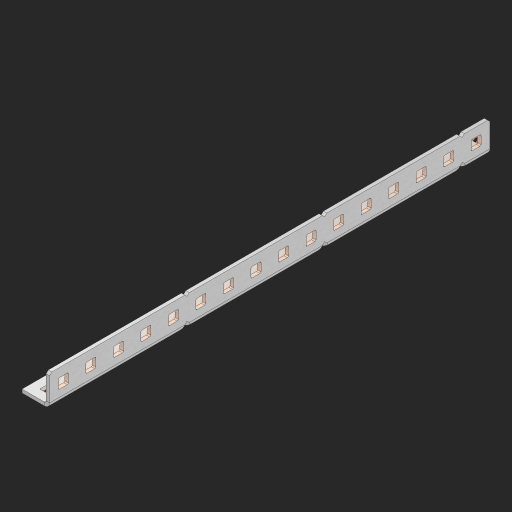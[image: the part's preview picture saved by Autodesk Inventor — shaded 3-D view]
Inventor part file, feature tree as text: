
AUTODESK INVENTOR PART (.ipt)
format: ipt  version: 2023 (Build 270158000, 158)  size: 696,832 bytes
history: native  units: in
note: dims shown in document units (in); Inventor stores cm internally (conversion verified against a paired STEP export)
features: other x37, extrude x31, sheet_metal_op x10, sketch x8, mirror x1, pattern_linear x1, chamfer x1
ambient origin geometry x8: Origin, YZ Plane, XZ Plane, XY Plane, X Axis, Y Axis, Z Axis, Center Point
bodies: Solid1 (feature_tree), Body (feature_tree)
feature tree (89):
  other  "Flange Pattern Plane"
  sheet_metal_op  "Flange Pattern"
  sheet_metal_op  "Body Pattern"
  other  "Arc Length"
  mirror  "Notch Mirror"
  pattern_linear  "Notch Pattern"  Spacing1=0.25in  [1 undecoded]
  chamfer  "End Chamfer"
  extrude  "Half Cut"  Depth=0.0625in
  sketch  "Sketch1"  dims[d0=1.5in]
  other  "Plate1"
  sketch  "Sketch2"  dims[d1=8.0in]
  other  "Plate2"
  sheet_metal_op  "Bend1"
  sheet_metal_op  "Corner1"
  sketch  "Sketch3"  dims[d2=0.0625in]
  other  "Flange Pattern Sketch"
  sketch  "Sketch7"  dims[d3=0.0625in]
  other  "Srf1"
  other  "Srf2"
  sketch  "Sketch8"  dims[d4=0.0312in]
  sketch  "Sketch9"  dims[d5=0.125in]
  other  "Srf91"
  sheet_metal_op  "Body Pattern Sketch"
  other  "Srf92"
  sketch  "Sketch13"  dims[d6=0.0625in]
  sketch  "Sketch14"  dims[d7=0.5in d8=90.0deg d9=0.0312in d10=0.25in d11=0.0625in d12=0.0625in d16=0.182in d17=0.02in d18=0.0625in d19=0.0in d20=0.25in d21=0.25in d46=0.172in d47=1.0in d48=0.0in d49=0.182in d50=0.02in d51=0.25in d52=0.25in d53=0.0625in d54=0.0in d55=0.172in d56=1.0in d57=0.0in d60=6.2992in d62=0.5in d63=0.3937in d65=0.5in d85=0.1473in d86=0.1782in d88=0.04in d89=0.0625in d90=0.0in d91=0.04in d92=0.0491in d95=2.5in d96=0.04in d97=0.25in d98=45.0deg d101=0.0in d102=2.497in d131=0.5in d132=6.2992in d134=0.5in d139=0.5in]
  other  "Srf856"
  other  "Srf1310"
  other  "Srf1311"
  other  "Srf1312"
  other  "Srf1376"
  other  "Srf1377"
  other  "Srf1728"
  other  "Srf1755"
  other  "Srf1878"
  other  "Srf1879"
  other  "Srf1880"
  other  "Srf1881"
  other  "Srf1882"
  other  "Srf1883"
  other  "Srf1884"
  other  "Srf1885"
  other  "Srf1886"
  other  "Srf1887"
  other  "Srf1942"
  other  "Srf1943"
  other  "Srf1944"
  other  "Srf1945"
  other  "Srf1946"
  other  "Srf1947"
  other  "Srf1948"
  other  "Srf1949"
  other  "Srf1950"
  other  "Srf1951"
  sheet_metal_op  "Flange Stamp"
  sheet_metal_op  "Flange Circle"
  sheet_metal_op  "Body Stamp"
  sheet_metal_op  "Body Circle"
  sheet_metal_op  "Notch"
  extrude  "ExtrusionSrf2"  Depth=0.0625in
  extrude  "ExtrusionSrf92"  Depth=0.5in
  extrude  "ExtrusionSrf856"  Depth=0.02in
  extrude  "ExtrusionSrf1310"  Depth=0.0625in
  extrude  "ExtrusionSrf1311"  TaperAngle=0.0deg  [1 undecoded]
  extrude  "ExtrusionSrf1312"  Depth=0.5in
  extrude  "ExtrusionSrf1376"  Depth=0.5in
  extrude  "ExtrusionSrf1377"  Depth=0.5in
  extrude  "ExtrusionSrf1728"  Depth=0.5in TaperAngle=0.0deg
  extrude  "ExtrusionSrf1755"  Depth=0.5in
  extrude  "ExtrusionSrf1878"  Depth=0.02in
  extrude  "ExtrusionSrf1879"  Depth=0.5in
  extrude  "ExtrusionSrf1880"  Depth=0.5in
  extrude  "ExtrusionSrf1881"  Depth=0.0625in
  extrude  "ExtrusionSrf1882"  TaperAngle=0.0deg  [1 undecoded]
  extrude  "ExtrusionSrf1883"  Depth=0.5in
  extrude  "ExtrusionSrf1884"  Depth=0.5in TaperAngle=0.0deg
  extrude  "ExtrusionSrf1885"  Depth=0.5in
  extrude  "ExtrusionSrf1886"  Depth=0.5in
  extrude  "ExtrusionSrf1887"  Depth=0.5in
  extrude  "ExtrusionSrf1942"  Depth=0.5in
  extrude  "ExtrusionSrf1943"  Depth=0.5in
  extrude  "ExtrusionSrf1944"  Depth=0.0625in
  extrude  "ExtrusionSrf1945"  TaperAngle=0.0deg  [1 undecoded]
  extrude  "ExtrusionSrf1946"  Depth=0.5in
  extrude  "ExtrusionSrf1947"  Depth=0.5in
  extrude  "ExtrusionSrf1948"  Depth=0.5in
  extrude  "ExtrusionSrf1949"  Depth=0.5in TaperAngle=45.0deg
  extrude  "ExtrusionSrf1950"  TaperAngle=0.0deg  [1 undecoded]
  extrude  "ExtrusionSrf1951"  Depth=0.5in
note: 5 required parameter values undecoded (feature->parameter linkage not recoverable at this tier; creation-order binding heuristic only, values carry confidence <= 0.55)
